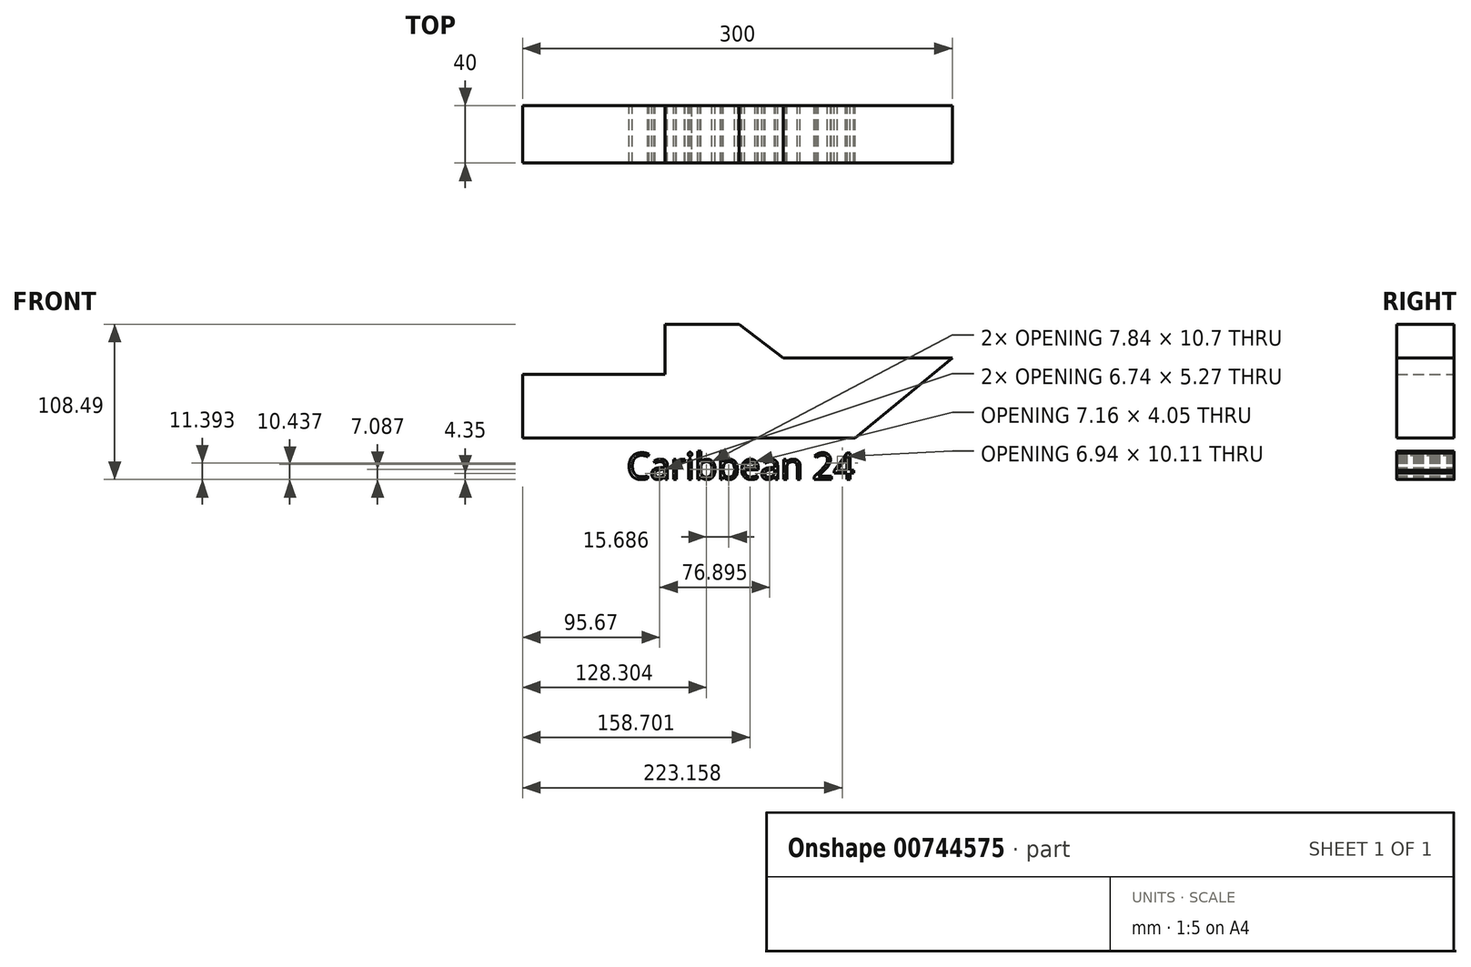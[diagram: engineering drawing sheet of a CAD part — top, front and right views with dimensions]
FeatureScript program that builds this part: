
annotation { "Feature Type Name" : "Feature", "Feature Type Description" : "" }
export const myFeature = defineFeature(function(context is Context, id is Id, definition is map)
    precondition{}
    {
        {
            var Q0;
            Q0=qCreatedBy(makeId("Front.planeOp"),FACE);
            var sketch = newSketch(context, id + "F0", { "sketchPlane" : qUnion([Q0])});
            skLineSegment(sketch, "E0.bottom", {"start": v(0, 0) * mm, "end": v(300, 0) * mm, "construction": true});
            skLineSegment(sketch, "E0.top", {"start": v(0, -200) * mm, "end": v(300, -200) * mm, "construction": true});
            skLineSegment(sketch, "E0.left", {"start": v(0, 0) * mm, "end": v(0, -200) * mm, "construction": true});
            skLineSegment(sketch, "E0.right", {"start": v(300, 0) * mm, "end": v(300, -200) * mm, "construction": true});
            skLineSegment(sketch, "E1", {"start": v(0, -165.33) * mm, "end": v(300, -165.33) * mm});
            skLineSegment(sketch, "E2", {"start": v(232.1, -165.33) * mm, "end": v(300, -109.53) * mm});
            skLineSegment(sketch, "E3", {"start": v(181.99, -109.53) * mm, "end": v(151.26, -85.9) * mm});
            skLineSegment(sketch, "E4", {"start": v(151.26, -85.9) * mm, "end": v(99.26, -85.9) * mm});
            skLineSegment(sketch, "E5", {"start": v(99.26, -85.9) * mm, "end": v(99.26, -120.88) * mm});
            skLineSegment(sketch, "E6", {"start": v(99.26, -120.88) * mm, "end": v(0, -120.88) * mm});
            skLineSegment(sketch, "E7", {"start": v(181.99, -109.53) * mm, "end": v(300, -109.53) * mm});
            skLineSegment(sketch, "E8", {"start": v(0, -120.88) * mm, "end": v(0, -165.33) * mm});
            skText(sketch, "E9", { "text": "Caribbean 24", "fontName": "OpenSans-Regular.ttf"});
            const initialGuessF0  = {"E9": [0.0728, -0.19414, 1, 0, 0.01843]};
            skSetInitialGuess(sketch, initialGuessF0);
            skSolve(sketch);
        }
        {
            var Q0;
            Q0 = qSketchRegion(id + "F0", true);
            extrude(context, id + "F1", {"entities" : qUnion([Q0]), "depth" : 40 * mm, "offsetDistance" : 25 * mm});
        }
    });
